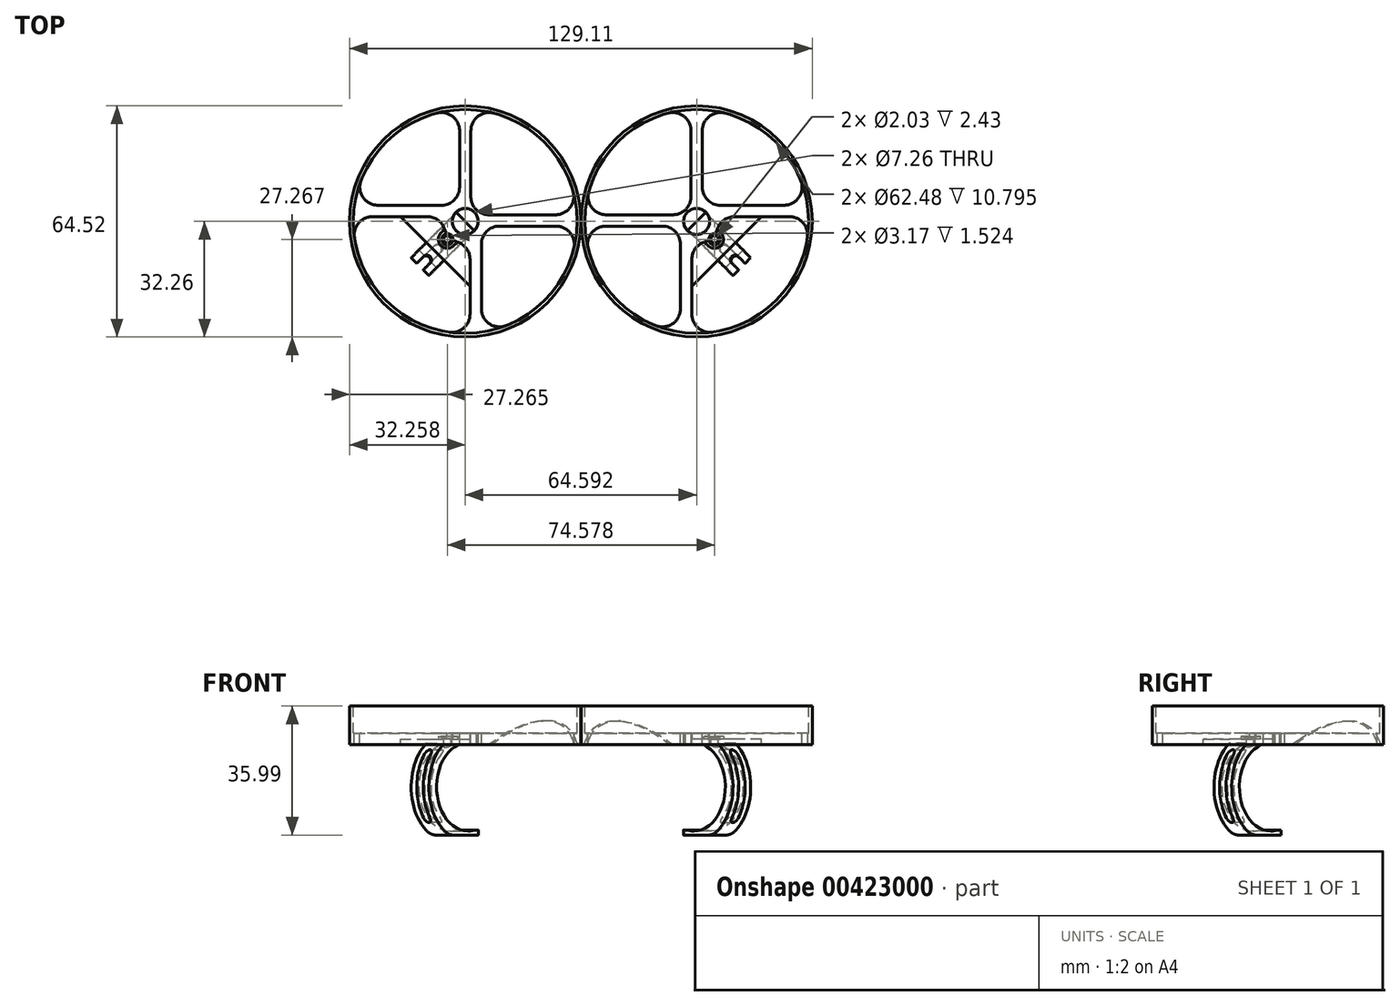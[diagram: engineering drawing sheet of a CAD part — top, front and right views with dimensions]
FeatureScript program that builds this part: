
annotation { "Feature Type Name" : "Feature", "Feature Type Description" : "" }
export const myFeature = defineFeature(function(context is Context, id is Id, definition is map)
    precondition{}
    {
        {
            var Q0;
            Q0=qCreatedBy(makeId("Top.planeOp"),FACE);
            var sketch = newSketch(context, id + "F0", { "sketchPlane" : qUnion([Q0])});
            skCircle(sketch, "E0", {"center": v(0, 0) * mm, "radius": 3.63 * mm});
            skCircle(sketch, "E1", {"center": v(0, 0) * mm, "radius": 32.26 * mm});
            skArc(sketch, "E2", {"start": v(-23.01, -21.13) * mm, "mid": v(0, -31.24) * mm, "end": v(23.01, -21.13) * mm});
            skLineSegment(sketch, "E3", {"start": v(4.3, 2.07) * mm, "end": v(25.05, -18.67) * mm});
            skLineSegment(sketch, "E4", {"start": v(-4.12, 2.26) * mm, "end": v(-25.05, -18.67) * mm});
            skArc(sketch, "E5.trimOffspring", {"start": v(25.05, -18.67) * mm, "mid": v(31.2, 1.47) * mm, "end": v(23.18, 20.95) * mm});
            skLineSegment(sketch, "E6", {"start": v(0, 14.05) * mm, "end": v(0, -14.19) * mm, "construction": true});
            skLineSegment(sketch, "E7", {"start": v(-13.71, -11.83) * mm, "end": v(13.71, -11.83) * mm});
            skLineSegment(sketch, "E8", {"start": v(-23.02, -21.13) * mm, "end": v(-13.71, -11.83) * mm});
            skLineSegment(sketch, "E9", {"start": v(23.01, -21.13) * mm, "end": v(13.71, -11.83) * mm});
            skArc(sketch, "E10.trimOffspring", {"start": v(-1.59, 31.2) * mm, "mid": v(-11.83, 28.92) * mm, "end": v(-20.74, 23.37) * mm});
            skLineSegment(sketch, "E11", {"start": v(-20.74, 23.37) * mm, "end": v(-1.59, 4.22) * mm});
            skLineSegment(sketch, "E12", {"start": v(-4.12, 2.26) * mm, "end": v(-23, 21.14) * mm});
            skLineSegment(sketch, "E13", {"start": v(20.95, 23.18) * mm, "end": v(1.87, 4.1) * mm});
            skLineSegment(sketch, "E14", {"start": v(4.3, 2.07) * mm, "end": v(23.18, 20.95) * mm});
            skArc(sketch, "E15", {"start": v(1.87, 4.1) * mm, "mid": v(0.15, 4.5) * mm, "end": v(-1.59, 4.22) * mm});
            skArc(sketch, "E16.trimOffspring", {"start": v(20.95, 23.18) * mm, "mid": v(11.96, 28.86) * mm, "end": v(1.59, 31.2) * mm});
            skArc(sketch, "E17.trimOffspring", {"start": v(-23, 21.14) * mm, "mid": v(-31.2, 1.6) * mm, "end": v(-25.05, -18.67) * mm});
            skLineSegment(sketch, "E18", {"start": v(1.59, 31.2) * mm, "end": v(-1.59, 31.2) * mm});
            skSolve(sketch);
        }
        {
            var Q0;
            Q0=qSketchRegion(id+"F0",true);
            extrude(context, id + "F1", {"entities" : qUnion([Q0]), "oppositeDirection" : true, "depth" : 3.17 * mm});
        }
        {
            var Q0;
            Q0=qCreatedBy(makeId("Right.planeOp"),FACE);
            cPlane(context, id + "F2", {"entities" : qUnion([Q0]), "cplaneType" : CPlaneType.OFFSET, "offset" : 0 * mm, "width" : 152.4 * mm, "height" : 152.4 * mm});
        }
        {
            var Q0;
            Q0=qCreatedBy(id+"F2.planeOp",FACE);
            var sketch = newSketch(context, id + "F3", { "sketchPlane" : qUnion([Q0])});
            skArc(sketch, "E19", {"start": v(-6.17, -3.18) * mm, "mid": v(-14.41, -18.02) * mm, "end": v(0, -27) * mm});
            skArc(sketch, "E20.0", {"start": v(-11.83, -2.73) * mm, "mid": v(-17.85, -14.83) * mm, "end": v(-11.99, -27) * mm});
            skLineSegment(sketch, "E21", {"start": v(0, -27) * mm, "end": v(3.73, -27) * mm});
            skLineSegment(sketch, "E22", {"start": v(3.73, -27) * mm, "end": v(3.73, -28.37) * mm});
            skLineSegment(sketch, "E23", {"start": v(3.73, -28.37) * mm, "end": v(-8.06, -28.37) * mm});
            skPoint(sketch, "E24.visualSharp", {"position": v(-9.94, -28.37) * mm});
            skArc(sketch, "E24.filletArc", {"start": v(-11.99, -27) * mm, "mid": v(-10.14, -28.02) * mm, "end": v(-8.06, -28.37) * mm});
            skLineSegment(sketch, "E25", {"start": v(-6.17, -3.18) * mm, "end": v(-6.17, -2.73) * mm});
            skLineSegment(sketch, "E26", {"start": v(-6.17, -2.73) * mm, "end": v(-11.83, -2.73) * mm});
            skSolve(sketch);
        }
        {
            var Q0;
            Q0=qSketchRegion(id+"F3",true);
            extrude(context, id + "F4", {"entities" : qUnion([Q0]), "operationType" : NewBodyOperationType.ADD, "endBound" : BoundingType.SYMMETRIC, "depth" : 7 * mm});
        }
        {
            var Q0;
            Q0=qCreatedBy(makeId("Front.planeOp"),FACE);
            var sketch = newSketch(context, id + "F5", { "sketchPlane" : qUnion([Q0])});
            skLineSegment(sketch, "E27.bottom", {"start": v(1.27, -4.57) * mm, "end": v(-1.27, -4.57) * mm});
            skLineSegment(sketch, "E27.top", {"start": v(1.27, -24.9) * mm, "end": v(-1.27, -24.9) * mm});
            skLineSegment(sketch, "E27.left", {"start": v(1.27, -4.57) * mm, "end": v(1.27, -24.9) * mm});
            skLineSegment(sketch, "E27.right", {"start": v(-1.27, -4.57) * mm, "end": v(-1.27, -24.9) * mm});
            skSolve(sketch);
        }
        {
            var Q0;
            Q0=qSketchRegion(id+"F5",true);
            extrude(context, id + "F6", {"entities" : qUnion([Q0]), "operationType" : NewBodyOperationType.REMOVE, "depth" : 25.4 * mm});
        }
        {
            var Q0;
            Q0=makeQuery(id+"F6.boolean.opBoolean","COPY",EDGE,{"derivedFrom":makeQuery(id+"F6.opExtrude","SWEPT_EDGE",EDGE,{"disambiguationData":[OSD([sQuery(id+"F5.wireOp",EDGE,"E27.bottom"),sQuery(id+"F5.wireOp",EDGE,"E27.left")])]})});
            var Q1;
            Q1=makeQuery(id+"F6.boolean.opBoolean","COPY",EDGE,{"derivedFrom":makeQuery(id+"F6.opExtrude","SWEPT_EDGE",EDGE,{"disambiguationData":[OSD([sQuery(id+"F5.wireOp",EDGE,"E27.bottom"),sQuery(id+"F5.wireOp",EDGE,"E27.right")])]})});
            var Q2;
            Q2=makeQuery(id+"F6.boolean.opBoolean","COPY",EDGE,{"derivedFrom":makeQuery(id+"F6.opExtrude","SWEPT_EDGE",EDGE,{"disambiguationData":[OSD([sQuery(id+"F5.wireOp",EDGE,"E27.top"),sQuery(id+"F5.wireOp",EDGE,"E27.left")])]})});
            var Q3;
            Q3=makeQuery(id+"F6.boolean.opBoolean","COPY",EDGE,{"derivedFrom":makeQuery(id+"F6.opExtrude","SWEPT_EDGE",EDGE,{"disambiguationData":[OSD([sQuery(id+"F5.wireOp",EDGE,"E27.top"),sQuery(id+"F5.wireOp",EDGE,"E27.right")])]})});
            fillet(context, id + "F7", {"entities" : qUnion([Q0, Q1, Q2, Q3]), "radius" : 1.27 * mm, "tangentPropagation" : true, "allowEdgeOverflow" : false});
        }
        {
            var Q0;
            Q0=makeQuery(id+"F4.opExtrude","CAP_EDGE",EDGE,{"disambiguationData":[OSD([sQuery(id+"F3.wireOp",EDGE,"E22")])],"isStart":true});
            var Q1;
            Q1=makeQuery(id+"F4.opExtrude","CAP_EDGE",EDGE,{"disambiguationData":[OSD([sQuery(id+"F3.wireOp",EDGE,"E22")])],"isStart":false});
            fillet(context, id + "F8", {"entities" : qUnion([Q0, Q1]), "radius" : 3.48 * mm, "tangentPropagation" : true, "allowEdgeOverflow" : false});
        }
        {
            var Q0;
            Q0=makeQuery(id+"F1.opExtrude","CAP_FACE",FACE,{"disambiguationData":[OSD([sQuery(id+"F0.wireOp",EDGE,"nHin777B-PrCo-Cay2-vQFo-KD3bro2OhY4N"),sQuery(id+"F0.wireOp",EDGE,"E0"),sQuery(id+"F0.wireOp",EDGE,"E1"),sQuery(id+"F0.wireOp",EDGE,"E2"),sQuery(id+"F0.wireOp",EDGE,"E3"),sQuery(id+"F0.wireOp",EDGE,"3Kbo6qPl-UeJc-SpGb-QunT-igpGF68ZOVeu"),sQuery(id+"F0.wireOp",EDGE,"E4"),sQuery(id+"F0.wireOp",EDGE,"UkC3B4rK-ZQAm-ILdF-c06i-0da9ncZ2dpg8"),sQuery(id+"F0.wireOp",EDGE,"E5.trimOffspring"),sQuery(id+"F0.wireOp",EDGE,"E7")])],"isStart":true});
            var sketch = newSketch(context, id + "F9", { "sketchPlane" : qUnion([Q0])});
            skCircle(sketch, "E28", {"center": v(0, 0) * mm, "radius": 32.26 * mm});
            skCircle(sketch, "E29", {"center": v(0, 0) * mm, "radius": 31.24 * mm});
            skSolve(sketch);
        }
        {
            var Q0;
            Q0=qSketchRegion(id+"F9",true);
            extrude(context, id + "F10", {"entities" : qUnion([Q0]), "operationType" : NewBodyOperationType.ADD, "depth" : 7.62 * mm});
        }
        {
            var Q0;
            Q0=makeQuery(id+"F1.opExtrude","CAP_FACE",FACE,{"disambiguationData":[OSD([sQuery(id+"F0.wireOp",EDGE,"nHin777B-PrCo-Cay2-vQFo-KD3bro2OhY4N"),sQuery(id+"F0.wireOp",EDGE,"E0"),sQuery(id+"F0.wireOp",EDGE,"E1"),sQuery(id+"F0.wireOp",EDGE,"E3"),sQuery(id+"F0.wireOp",EDGE,"E4"),sQuery(id+"F0.wireOp",EDGE,"E7"),sQuery(id+"F0.wireOp",EDGE,"E8"),sQuery(id+"F0.wireOp",EDGE,"E9"),sQuery(id+"F0.wireOp",EDGE,"E5.trimOffspring"),sQuery(id+"F0.wireOp",EDGE,"E2"),sQuery(id+"F0.wireOp",EDGE,"QOe3KQ39-ohuL-hj8G-rkRm-wSydNN2H0yif"),sQuery(id+"F0.wireOp",EDGE,"tk3Uaz92-GOGT-vkV1-RqLY-bDL5NIjiCGRt"),sQuery(id+"F0.wireOp",EDGE,"E10.trimOffspring"),sQuery(id+"F0.wireOp",EDGE,"aa96e5e9-2f11-4529-9c6b-044ce098bced.trimOffspring")])],"isStart":true});
            var sketch = newSketch(context, id + "F11", { "sketchPlane" : qUnion([Q0])});
            skLineSegment(sketch, "E30", {"start": v(-13.71, -11.83) * mm, "end": v(-5.18, -3.3) * mm});
            skLineSegment(sketch, "E31", {"start": v(-13.71, -13.73) * mm, "end": v(-13.71, -11.83) * mm});
            skLineSegment(sketch, "E32", {"start": v(13.71, -11.83) * mm, "end": v(5.18, -3.3) * mm});
            skLineSegment(sketch, "E33", {"start": v(13.71, -11.83) * mm, "end": v(13.71, -11.83) * mm});
            skArc(sketch, "E34", {"start": v(-5.18, -3.3) * mm, "mid": v(0, -6.14) * mm, "end": v(5.18, -3.3) * mm});
            skLineSegment(sketch, "E35", {"start": v(-13.71, -13.73) * mm, "end": v(13.71, -11.83) * mm});
            skSolve(sketch);
        }
        {
            var Q0;
            Q0=qSketchRegion(id+"F11",true);
            extrude(context, id + "F12", {"entities" : qUnion([Q0]), "operationType" : NewBodyOperationType.REMOVE, "oppositeDirection" : true, "depth" : 1.57 * mm});
        }
        {
            var Q0;
            Q0=makeQuery(id+"F1.opExtrude","SWEPT_EDGE",EDGE,{"disambiguationData":[OSD([sQuery(id+"F0.wireOp",EDGE,"nHin777B-PrCo-Cay2-vQFo-KD3bro2OhY4N"),sQuery(id+"F0.wireOp",EDGE,"tk3Uaz92-GOGT-vkV1-RqLY-bDL5NIjiCGRt")])]});
            var Q1;
            Q1=makeQuery(id+"F1.opExtrude","SWEPT_EDGE",EDGE,{"disambiguationData":[OSD([sQuery(id+"F0.wireOp",EDGE,"QOe3KQ39-ohuL-hj8G-rkRm-wSydNN2H0yif"),sQuery(id+"F0.wireOp",EDGE,"aa96e5e9-2f11-4529-9c6b-044ce098bced.trimOffspring")])]});
            var Q2;
            Q2=makeQuery(id+"F12.boolean.opBoolean","COPY",EDGE,{"derivedFrom":makeQuery(id+"F12.opExtrude","SWEPT_EDGE",EDGE,{"disambiguationData":[OSD([sQuery(id+"F11.wireOp",EDGE,"E32"),sQuery(id+"F11.wireOp",EDGE,"E34")])]})});
            var Q3;
            Q3=makeQuery(id+"F12.boolean.opBoolean","COPY",EDGE,{"derivedFrom":makeQuery(id+"F12.opExtrude","SWEPT_EDGE",EDGE,{"disambiguationData":[OSD([sQuery(id+"F11.wireOp",EDGE,"E30"),sQuery(id+"F11.wireOp",EDGE,"E34")])]})});
            var Q4;
            Q4=makeQuery(id+"F1.opExtrude","SWEPT_EDGE",EDGE,{"disambiguationData":[OSD([sQuery(id+"F0.wireOp",EDGE,"E5.trimOffspring"),sQuery(id+"F0.wireOp",EDGE,"tk3Uaz92-GOGT-vkV1-RqLY-bDL5NIjiCGRt")])]});
            var Q5;
            Q5=makeQuery(id+"F1.opExtrude","SWEPT_EDGE",EDGE,{"disambiguationData":[OSD([sQuery(id+"F0.wireOp",EDGE,"QOe3KQ39-ohuL-hj8G-rkRm-wSydNN2H0yif"),sQuery(id+"F0.wireOp",EDGE,"E10.trimOffspring")])]});
            var Q6;
            Q6=makeQuery(id+"F1.opExtrude","SWEPT_EDGE",EDGE,{"disambiguationData":[OSD([sQuery(id+"F0.wireOp",EDGE,"E8"),sQuery(id+"F0.wireOp",EDGE,"E2")])]});
            var Q7;
            Q7=makeQuery(id+"F1.opExtrude","SWEPT_EDGE",EDGE,{"disambiguationData":[OSD([sQuery(id+"F0.wireOp",EDGE,"E4"),sQuery(id+"F0.wireOp",EDGE,"E10.trimOffspring")])]});
            var Q8;
            Q8=makeQuery(id+"F1.opExtrude","SWEPT_EDGE",EDGE,{"disambiguationData":[OSD([sQuery(id+"F0.wireOp",EDGE,"E9"),sQuery(id+"F0.wireOp",EDGE,"E2")])]});
            var Q9;
            Q9=makeQuery(id+"F1.opExtrude","SWEPT_EDGE",EDGE,{"disambiguationData":[OSD([sQuery(id+"F0.wireOp",EDGE,"E3"),sQuery(id+"F0.wireOp",EDGE,"E5.trimOffspring")])]});
            var Q10;
            Q10=makeQuery(id+"F1.opExtrude","SWEPT_EDGE",EDGE,{"disambiguationData":[OSD([sQuery(id+"F0.wireOp",EDGE,"E12"),sQuery(id+"F0.wireOp",EDGE,"E17.trimOffspring")])]});
            var Q11;
            Q11=makeQuery(id+"F1.opExtrude","SWEPT_EDGE",EDGE,{"disambiguationData":[OSD([sQuery(id+"F0.wireOp",EDGE,"E13"),sQuery(id+"F0.wireOp",EDGE,"E16.trimOffspring")])]});
            var Q12;
            Q12=makeQuery(id+"F1.opExtrude","SWEPT_EDGE",EDGE,{"disambiguationData":[OSD([sQuery(id+"F0.wireOp",EDGE,"E3"),sQuery(id+"F0.wireOp",EDGE,"E14")])]});
            var Q13;
            Q13=makeQuery(id+"F1.opExtrude","SWEPT_EDGE",EDGE,{"disambiguationData":[OSD([sQuery(id+"F0.wireOp",EDGE,"E13"),sQuery(id+"F0.wireOp",EDGE,"E15")])]});
            var Q14;
            Q14=makeQuery(id+"F1.opExtrude","SWEPT_EDGE",EDGE,{"disambiguationData":[OSD([sQuery(id+"F0.wireOp",EDGE,"E11"),sQuery(id+"F0.wireOp",EDGE,"E15")])]});
            fillet(context, id + "F13", {"entities" : qUnion([Q0, Q1, Q2, Q3, Q4, Q5, Q6, Q7, Q8, Q9, Q10, Q11, Q12, Q13, Q14]), "radius" : 5.08 * mm, "tangentPropagation" : true, "allowEdgeOverflow" : false});
        }
        {
            var Q0;
            Q0=makeQuery(id+"F12.boolean.opBoolean","COPY",FACE,{"derivedFrom":makeQuery(id+"F12.opExtrude","CAP_FACE",FACE,{"disambiguationData":[OSD([sQuery(id+"F11.wireOp",EDGE,"E30"),sQuery(id+"F11.wireOp",EDGE,"E31"),sQuery(id+"F11.wireOp",EDGE,"E32"),sQuery(id+"F11.wireOp",EDGE,"E33"),sQuery(id+"F11.wireOp",EDGE,"E34"),sQuery(id+"F11.wireOp",EDGE,"E35")])],"isStart":false})});
            var sketch = newSketch(context, id + "F14", { "sketchPlane" : qUnion([Q0])});
            skCircle(sketch, "E36", {"center": v(0, -7.06) * mm, "radius": 2.5 * mm});
            skPoint(sketch, "E36.centerSnap0", {"position": v(0, -6.14) * mm});
            skSolve(sketch);
        }
        {
            var Q0;
            Q0=qSketchRegion(id+"F14",true);
            extrude(context, id + "F15", {"entities" : qUnion([Q0]), "operationType" : NewBodyOperationType.ADD, "depth" : 0.76 * mm});
        }
        {
            var Q0;
            Q0=makeQuery(id+"F15.boolean.opBoolean","INTERSECT",EDGE,{"disambiguationData":[OD(0.0)],"derivedFrom":[makeQuery(id+"F12.boolean.opBoolean","COPY",FACE,{"derivedFrom":makeQuery(id+"F12.opExtrude","SWEPT_FACE",FACE,{"disambiguationData":[OSD([sQuery(id+"F11.wireOp",EDGE,"E34")])]})}),makeQuery(id+"F15.opExtrude","SWEPT_FACE",FACE,{"disambiguationData":[OSD([sQuery(id+"F14.wireOp",EDGE,"E36")])]})]});
            var Q1;
            Q1=makeQuery(id+"F15.boolean.opBoolean","INTERSECT",EDGE,{"disambiguationData":[OD(1.0)],"derivedFrom":[makeQuery(id+"F12.boolean.opBoolean","COPY",FACE,{"derivedFrom":makeQuery(id+"F12.opExtrude","SWEPT_FACE",FACE,{"disambiguationData":[OSD([sQuery(id+"F11.wireOp",EDGE,"E34")])]})}),makeQuery(id+"F15.opExtrude","SWEPT_FACE",FACE,{"disambiguationData":[OSD([sQuery(id+"F14.wireOp",EDGE,"E36")])]})]});
            fillet(context, id + "F16", {"entities" : qUnion([Q0, Q1]), "radius" : 5.08 * mm, "tangentPropagation" : true, "allowEdgeOverflow" : false});
        }
        {
            var Q0;
            Q0=makeQuery(id+"F1.opExtrude","CAP_FACE",FACE,{"disambiguationData":[OSD([sQuery(id+"F0.wireOp",EDGE,"nHin777B-PrCo-Cay2-vQFo-KD3bro2OhY4N"),sQuery(id+"F0.wireOp",EDGE,"E0"),sQuery(id+"F0.wireOp",EDGE,"E1"),sQuery(id+"F0.wireOp",EDGE,"E3"),sQuery(id+"F0.wireOp",EDGE,"E4"),sQuery(id+"F0.wireOp",EDGE,"E7"),sQuery(id+"F0.wireOp",EDGE,"E8"),sQuery(id+"F0.wireOp",EDGE,"E9"),sQuery(id+"F0.wireOp",EDGE,"E5.trimOffspring"),sQuery(id+"F0.wireOp",EDGE,"E2"),sQuery(id+"F0.wireOp",EDGE,"QOe3KQ39-ohuL-hj8G-rkRm-wSydNN2H0yif"),sQuery(id+"F0.wireOp",EDGE,"tk3Uaz92-GOGT-vkV1-RqLY-bDL5NIjiCGRt"),sQuery(id+"F0.wireOp",EDGE,"E10.trimOffspring"),sQuery(id+"F0.wireOp",EDGE,"aa96e5e9-2f11-4529-9c6b-044ce098bced.trimOffspring")])],"isStart":true});
            var sketch = newSketch(context, id + "F17", { "sketchPlane" : qUnion([Q0])});
            skCircle(sketch, "E37", {"center": v(0, -7.06) * mm, "radius": 1.02 * mm});
            skPoint(sketch, "E37.centerSnap0", {"position": v(0, -6.14) * mm});
            skSolve(sketch);
        }
        {
            var Q0;
            Q0=qSketchRegion(id+"F17",true);
            extrude(context, id + "F18", {"entities" : qUnion([Q0]), "operationType" : NewBodyOperationType.REMOVE, "oppositeDirection" : true, "depth" : 25.4 * mm});
        }
        {
            var Q0;
            Q0=makeQuery(id+"F1.opExtrude","CAP_FACE",FACE,{"disambiguationData":[OSD([sQuery(id+"F0.wireOp",EDGE,"nHin777B-PrCo-Cay2-vQFo-KD3bro2OhY4N"),sQuery(id+"F0.wireOp",EDGE,"E0"),sQuery(id+"F0.wireOp",EDGE,"E1"),sQuery(id+"F0.wireOp",EDGE,"E3"),sQuery(id+"F0.wireOp",EDGE,"E4"),sQuery(id+"F0.wireOp",EDGE,"E7"),sQuery(id+"F0.wireOp",EDGE,"E8"),sQuery(id+"F0.wireOp",EDGE,"E9"),sQuery(id+"F0.wireOp",EDGE,"E5.trimOffspring"),sQuery(id+"F0.wireOp",EDGE,"E2"),sQuery(id+"F0.wireOp",EDGE,"QOe3KQ39-ohuL-hj8G-rkRm-wSydNN2H0yif"),sQuery(id+"F0.wireOp",EDGE,"tk3Uaz92-GOGT-vkV1-RqLY-bDL5NIjiCGRt"),sQuery(id+"F0.wireOp",EDGE,"E10.trimOffspring"),sQuery(id+"F0.wireOp",EDGE,"aa96e5e9-2f11-4529-9c6b-044ce098bced.trimOffspring")])],"isStart":true});
            var sketch = newSketch(context, id + "F19", { "sketchPlane" : qUnion([Q0])});
            skCircle(sketch, "E38", {"center": v(0, -7.06) * mm, "radius": 1.59 * mm});
            skSolve(sketch);
        }
        {
            var Q0;
            Q0=qSketchRegion(id+"F19",true);
            extrude(context, id + "F20", {"entities" : qUnion([Q0]), "operationType" : NewBodyOperationType.REMOVE, "oppositeDirection" : true, "depth" : 1.52 * mm});
        }
        {
            var Q0;
            Q0=qCreatedBy(makeId("Front.planeOp"),FACE);
            cPlane(context, id + "F21", {"entities" : qUnion([Q0]), "cplaneType" : CPlaneType.OFFSET, "offset" : 25.4 * mm, "oppositeDirection" : true, "width" : 152.4 * mm, "height" : 152.4 * mm});
        }
        {
            var Q0;
            Q0=qCreatedBy(id+"F21.planeOp",FACE);
            var sketch = newSketch(context, id + "F22", { "sketchPlane" : qUnion([Q0])});
            skCircle(sketch, "E39", {"center": v(0, -22.23) * mm, "radius": 25.4 * mm});
            skSolve(sketch);
        }
        {
            var Q0;
            Q0 = qSketchRegion(id + "F22", true);
            extrude(context, id + "F23", {"entities" : qUnion([Q0]), "operationType" : NewBodyOperationType.REMOVE, "oppositeDirection" : true, "depth" : 12.7 * mm, "hasDraft" : true, "draftAngle" : 3 * degree});
        }
        {
            var Q0;
            Q0=makeQuery(id+"F1.opExtrude","SWEPT_BODY",BODY,{"disambiguationData":[OSD([sQuery(id+"F0.wireOp",EDGE,"E0"),sQuery(id+"F0.wireOp",EDGE,"E1"),sQuery(id+"F0.wireOp",EDGE,"E3"),sQuery(id+"F0.wireOp",EDGE,"E4"),sQuery(id+"F0.wireOp",EDGE,"E7"),sQuery(id+"F0.wireOp",EDGE,"E8"),sQuery(id+"F0.wireOp",EDGE,"E9"),sQuery(id+"F0.wireOp",EDGE,"E5.trimOffspring"),sQuery(id+"F0.wireOp",EDGE,"E2"),sQuery(id+"F0.wireOp",EDGE,"E10.trimOffspring"),sQuery(id+"F0.wireOp",EDGE,"E11"),sQuery(id+"F0.wireOp",EDGE,"E12"),sQuery(id+"F0.wireOp",EDGE,"E13"),sQuery(id+"F0.wireOp",EDGE,"E14"),sQuery(id+"F0.wireOp",EDGE,"E15"),sQuery(id+"F0.wireOp",EDGE,"E16.trimOffspring"),sQuery(id+"F0.wireOp",EDGE,"E17.trimOffspring"),sQuery(id+"F0.wireOp",EDGE,"E18")])]});
            var Q1;
            Q1=makeQuery(id+"F1.opExtrude","CAP_EDGE",EDGE,{"disambiguationData":[OSD([sQuery(id+"F0.wireOp",EDGE,"E0")])],"isStart":false});
            transform(context, id + "F24", {"entities" : qUnion([Q0]), "transformType" : TransformType.ROTATION, "transformAxis" : qUnion([Q1]), "angle" : 45 * degree, "makeCopy" : false});
        }
        {
            var Q0;
            Q0=qCreatedBy(makeId("Right.planeOp"),FACE);
            cPlane(context, id + "F25", {"entities" : qUnion([Q0]), "cplaneType" : CPlaneType.OFFSET, "offset" : 32.3 * mm, "oppositeDirection" : true, "width" : 152.4 * mm, "height" : 152.4 * mm});
        }
        {
            var Q0;
            Q0=makeQuery(id+"F1.opExtrude","SWEPT_BODY",BODY,{"disambiguationData":[OSD([sQuery(id+"F0.wireOp",EDGE,"E0"),sQuery(id+"F0.wireOp",EDGE,"E1"),sQuery(id+"F0.wireOp",EDGE,"E3"),sQuery(id+"F0.wireOp",EDGE,"E4"),sQuery(id+"F0.wireOp",EDGE,"E7"),sQuery(id+"F0.wireOp",EDGE,"E8"),sQuery(id+"F0.wireOp",EDGE,"E9"),sQuery(id+"F0.wireOp",EDGE,"E5.trimOffspring"),sQuery(id+"F0.wireOp",EDGE,"E2"),sQuery(id+"F0.wireOp",EDGE,"E10.trimOffspring"),sQuery(id+"F0.wireOp",EDGE,"E11"),sQuery(id+"F0.wireOp",EDGE,"E12"),sQuery(id+"F0.wireOp",EDGE,"E13"),sQuery(id+"F0.wireOp",EDGE,"E14"),sQuery(id+"F0.wireOp",EDGE,"E15"),sQuery(id+"F0.wireOp",EDGE,"E16.trimOffspring"),sQuery(id+"F0.wireOp",EDGE,"E17.trimOffspring"),sQuery(id+"F0.wireOp",EDGE,"E18")])]});
            var Q1;
            Q1=qCreatedBy(id+"F25.planeOp",FACE);
            mirror(context, id + "F26", {"entities" : qUnion([Q0]), "mirrorPlane" : qUnion([Q1])});
        }
    });
